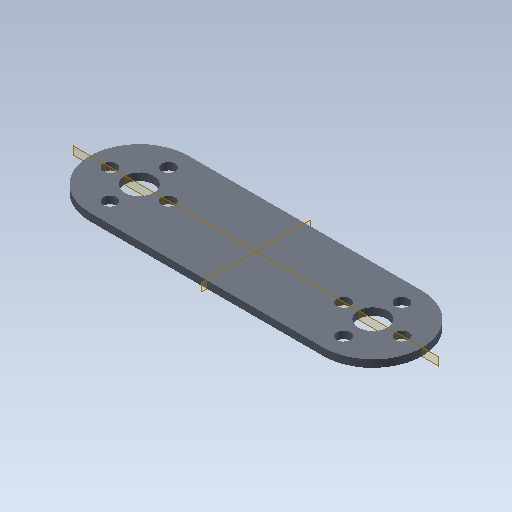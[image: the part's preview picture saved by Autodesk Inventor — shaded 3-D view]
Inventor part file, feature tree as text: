
AUTODESK INVENTOR PART (.ipt)
format: ipt  version: 2020 (Build 240168000, 168)  size: 151,040 bytes
history: native  units: in
note: dims shown in document units (in); Inventor stores cm internally (conversion verified against a paired STEP export)
features: other x15, plane x2, imported_body x1
ambient origin geometry x8: Origin, YZ Plane, XZ Plane, XY Plane, X Axis, Y Axis, Z Axis, Center Point
bodies: Body1 (feature_tree)
feature tree (18):
  other  "tetrix_739061_2012"
  other  "tetrix_739061_20121"
  other  "A_1"
  other  "A_2"
  other  "A_3"
  other  "A_4"
  other  "A_5"
  other  "A_6"
  other  "A_7"
  other  "A_8"
  other  "A_9"
  other  "A_10"
  other  "FRONT"
  other  "TOP"
  other  "RIGHT"
  plane  "Work Plane4"
  plane  "Work Plane5"
  imported_body  "Base1"
